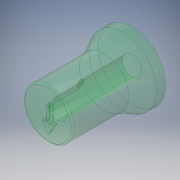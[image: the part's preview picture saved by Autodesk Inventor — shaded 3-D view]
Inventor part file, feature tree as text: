
AUTODESK INVENTOR PART (.ipt)
format: ipt  version: 2017 SP1 (Build 210196100, 196)  size: 163,840 bytes
history: native  units: in
note: dims shown in document units (in); Inventor stores cm internally (conversion verified against a paired STEP export)
features: extrude x5, sketch x5, chamfer x2, projected_geometry x1
ambient origin geometry x8: Origin, YZ Plane, XZ Plane, XY Plane, X Axis, Y Axis, Z Axis, Center Point
bodies: Solid1 (feature_tree)
feature tree (13):
  extrude  "Extrusion1"  Depth=0.0125in
  extrude  "Extrusion2"  Depth=0.2in
  extrude  "Extrusion3"  Depth=0.2in
  chamfer  "Chamfer1"  Distance=0.05in
  extrude  "Extrusion6"  Depth=0.125in TaperAngle=45.0deg
  extrude  "Extrusion10"  TaperAngle=60.0deg  [1 undecoded]
  chamfer  "Chamfer3"  Distance=0.215in
  sketch  "Sketch1"  dims[d0=0.235in d2=0.0125in]
  sketch  "Sketch2"  dims[d3=1.0in d4=0.0in d5=0.2in]
  sketch  "Sketch3"  dims[d6=0.125in d7=0.0in d8=0.2in]
  sketch  "Sketch6"  dims[d10=0.05in]
  projected_geometry  "Projected Loop4"
  sketch  "Sketch10"  dims[d11=0.15in d12=0.05in d13=0.0in d20=0.02in d21=0.125in d22=45.0deg d24=60.0deg d26=0.215in d27=0.4in d28=0.0in d45=0.1333in d49=0.5in d50=0.2in d51=0.2in d52=0.125in d53=0.0in d54=0.25in d55=0.12in d56=45.0deg]
note: 1 required parameter value undecoded (feature->parameter linkage not recoverable at this tier; creation-order binding heuristic only, values carry confidence <= 0.55)
